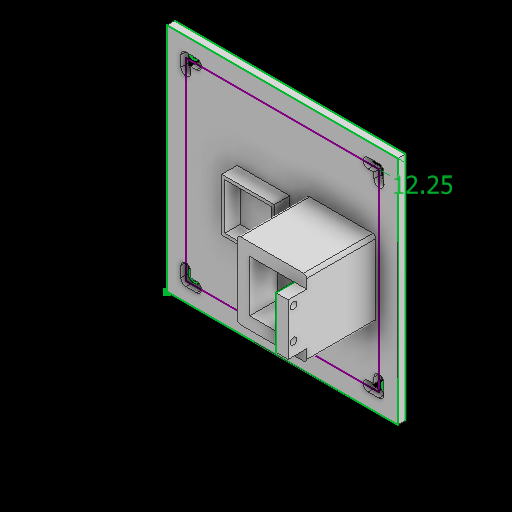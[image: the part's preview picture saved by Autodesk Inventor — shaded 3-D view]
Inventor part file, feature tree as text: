
AUTODESK INVENTOR PART (.ipt)
format: ipt  version: 2025.1 (Build 291241000, 241)  size: 286,208 bytes
history: native  units: in
note: dims shown in document units (in); Inventor stores cm internally (conversion verified against a paired STEP export)
features: sketch x16, extrude x9, projected_geometry x5, other x3, fillet x1
ambient origin geometry x8: Origin, YZ Plane, XZ Plane, XY Plane, X Axis, Y Axis, Z Axis, Center Point
bodies: Body1 (feature_tree)
feature tree (34):
  other  "솔리드1"
  extrude  "돌출1"  Depth=5.9055in
  sketch  "스케치2"
  extrude  "돌출3"  Depth=5.9055in
  sketch  "스케치8"
  sketch  "스케치9"
  sketch  "스케치10"
  extrude  "돌출7"  Depth=0.1969in TaperAngle=0.0deg
  extrude  "돌출8"  Depth=0.4823in
  extrude  "돌출9"  Depth=0.4823in
  extrude  "돌출10"  Depth=0.2559in
  extrude  "돌출11"  Depth=4.9409in
  sketch  "스케치16"
  sketch  "스케치17"
  extrude  "돌출12"  Depth=4.9409in
  sketch  "스케치19"
  fillet  "모깎기3"  Radius=0.1378in
  extrude  "돌출13"  Depth=0.2756in
  sketch  "스케치1"
  projected_geometry  "투영된 루프1"
  sketch  "스케치4"
  projected_geometry  "투영된 루프2"
  other  "스케치 - 직사각형 패턴3"
  other  "스케치 - 직사각형 패턴4"
  projected_geometry  "투영된 루프4"
  sketch  "스케치11"
  sketch  "스케치12"
  sketch  "스케치13"
  sketch  "스케치14"
  projected_geometry  "투영된 루프5"
  sketch  "스케치15"
  projected_geometry  "투영된 루프6"
  sketch  "스케치18"
  sketch  "스케치20"
